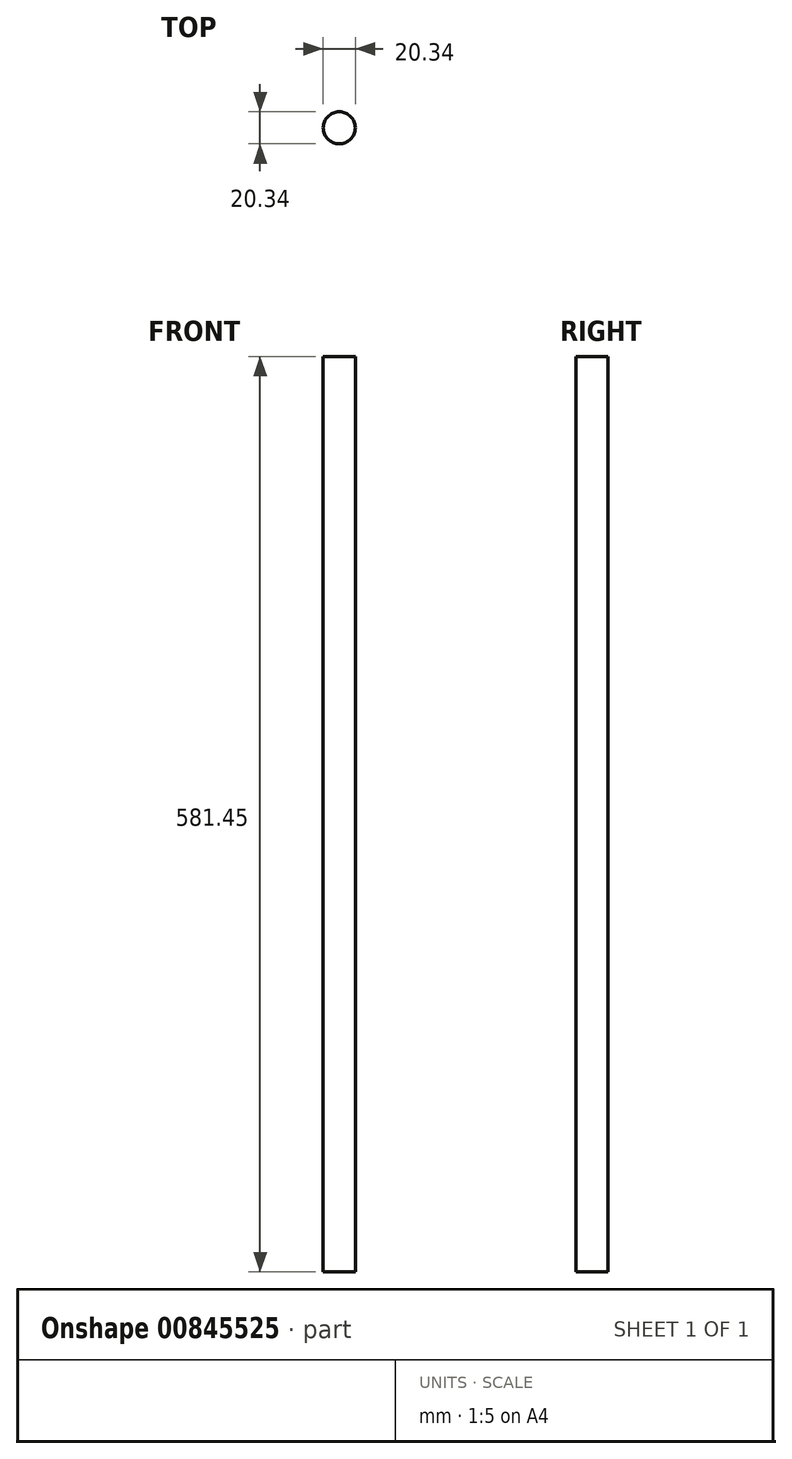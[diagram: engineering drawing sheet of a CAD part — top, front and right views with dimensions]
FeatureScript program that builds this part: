
annotation { "Feature Type Name" : "Feature", "Feature Type Description" : "" }
export const myFeature = defineFeature(function(context is Context, id is Id, definition is map)
    precondition{}
    {
        {
            var Q0;
            Q0=qCreatedBy(makeId("Top.planeOp"),FACE);
            var sketch = newSketch(context, id + "F0", { "sketchPlane" : qUnion([Q0])});
            skCircle(sketch, "E0", {"center": v(0, 0) * mm, "radius": 10.17 * mm});
            skSolve(sketch);
        }
        {
            var Q0;
            Q0 = qSketchRegion(id + "F0", true);
            extrude(context, id + "F1", {"entities" : qUnion([Q0]), "depth" : 581.45 * mm, "offsetDistance" : 25.4 * mm});
        }
    });
